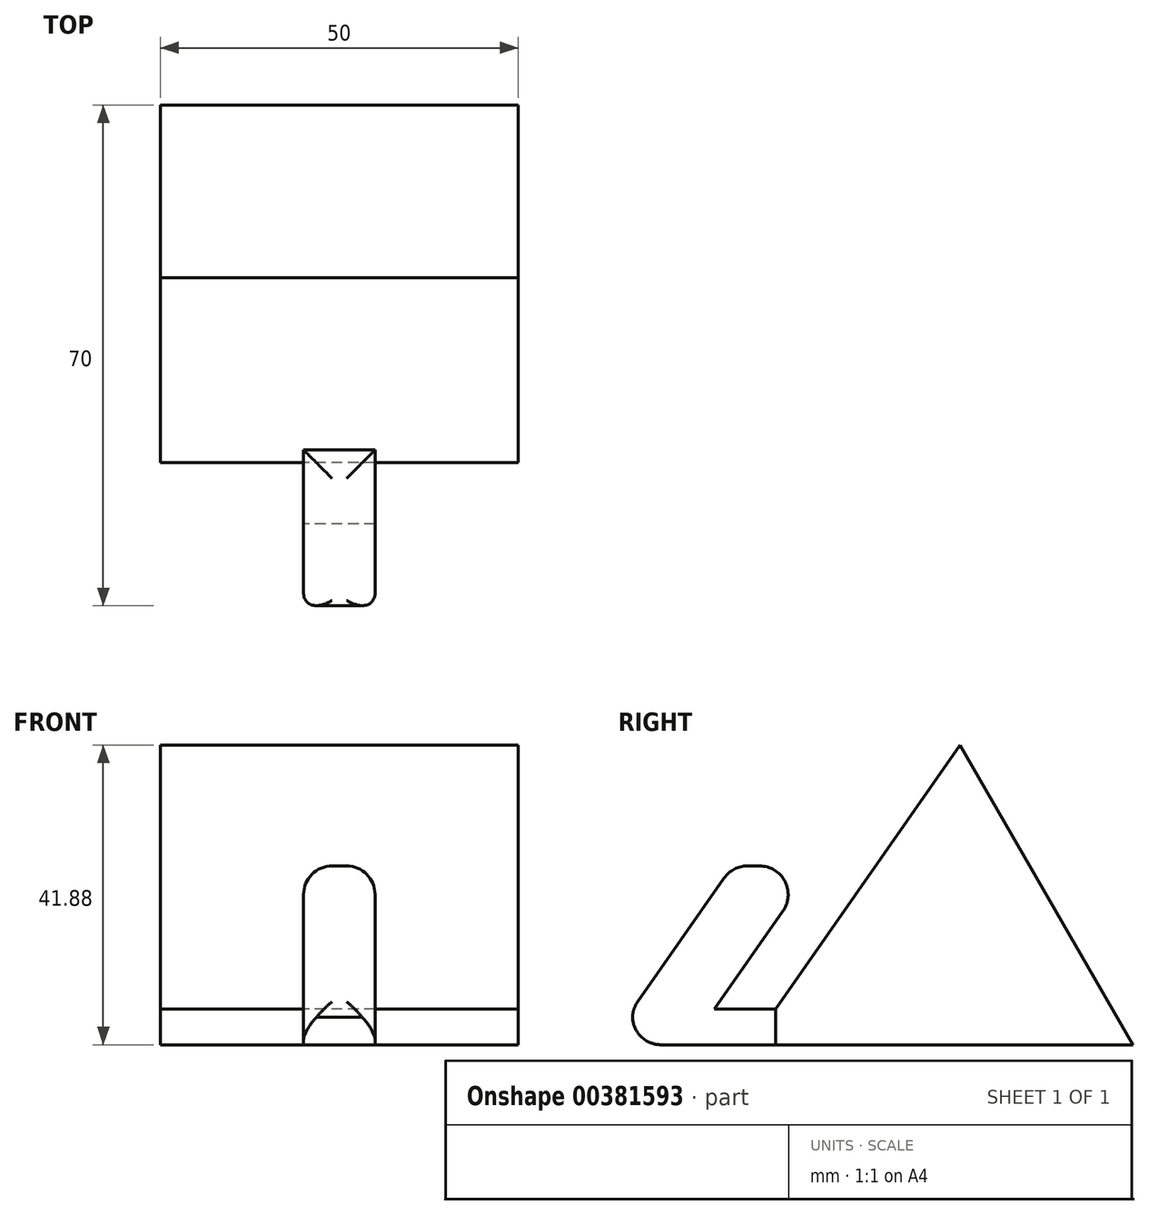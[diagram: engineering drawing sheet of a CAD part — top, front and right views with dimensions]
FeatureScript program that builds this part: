
annotation { "Feature Type Name" : "Feature", "Feature Type Description" : "" }
export const myFeature = defineFeature(function(context is Context, id is Id, definition is map)
    precondition{}
    {
        {
            var Q0;
            Q0=qCreatedBy(makeId("Right.planeOp"),FACE);
            var sketch = newSketch(context, id + "F0", { "sketchPlane" : qUnion([Q0])});
            skLineSegment(sketch, "E0.top", {"start": v(0, 5) * mm, "end": v(-8.55, 5) * mm});
            skPoint(sketch, "E0.middle", {"position": v(0, 0) * mm});
            skLineSegment(sketch, "E1", {"start": v(0, 5) * mm, "end": v(14, 25) * mm});
            skLineSegment(sketch, "E2", {"start": v(5.46, 25) * mm, "end": v(-8.55, 5) * mm});
            skLineSegment(sketch, "E3", {"start": v(-20, 5) * mm, "end": v(-6, 25) * mm});
            skLineSegment(sketch, "E4", {"start": v(-6, 25) * mm, "end": v(5.46, 25) * mm});
            skLineSegment(sketch, "E5", {"start": v(-20, 0) * mm, "end": v(0, 0) * mm});
            skLineSegment(sketch, "E6", {"start": v(50, 0) * mm, "end": v(0, 0) * mm});
            skLineSegment(sketch, "E7", {"start": v(-20, 0) * mm, "end": v(-20, 5) * mm});
            skLineSegment(sketch, "E8", {"start": v(14, 25) * mm, "end": v(25.82, 41.88) * mm});
            skLineSegment(sketch, "E9", {"start": v(25.82, 41.88) * mm, "end": v(50, 0) * mm});
            skLineSegment(sketch, "E10", {"start": v(0, 5) * mm, "end": v(0, 0) * mm});
            skSolve(sketch);
        }
        {
            var Q0;
            Q0=makeQuery(id+"F0.imprint","IMPRINT",FACE,{"disambiguationData":[TD([[makeQuery(id+"F0.imprint","IMPRINT",EDGE,{"derivedFrom":sQuery(id+"F0.wireOp",EDGE,"E0.top")}),1.0]])]});
            extrude(context, id + "F1", {"entities" : qUnion([Q0]), "endBound" : BoundingType.SYMMETRIC, "depth" : 10 * mm, "offsetDistance" : 25 * mm});
        }
        {
            var Q0;
            Q0=makeQuery(id+"F0.imprint","IMPRINT",FACE,{"disambiguationData":[TD([[makeQuery(id+"F0.imprint","IMPRINT",EDGE,{"derivedFrom":sQuery(id+"F0.wireOp",EDGE,"E1")}),-1.0]])]});
            extrude(context, id + "F2", {"entities" : qUnion([Q0]), "operationType" : NewBodyOperationType.ADD, "depth" : 25 * mm, "offsetDistance" : 25 * mm, "hasSecondDirection" : true, "secondDirectionOppositeDirection" : true, "secondDirectionDepth" : 25 * mm});
        }
        {
            var Q0;
            Q0=makeQuery(id+"F1.opExtrude","SWEPT_FACE",FACE,{"disambiguationData":[OSD([sQuery(id+"F0.wireOp",EDGE,"E3")])]});
            var Q1;
            Q1=makeQuery(id+"F1.opExtrude","SWEPT_FACE",FACE,{"disambiguationData":[OSD([sQuery(id+"F0.wireOp",EDGE,"E4")])]});
            var Q2;
            Q2=makeQuery(id+"F1.opExtrude","SWEPT_EDGE",EDGE,{"disambiguationData":[OSD([sQuery(id+"F0.wireOp",EDGE,"E5"),sQuery(id+"F0.wireOp",EDGE,"E7")])]});
            fillet(context, id + "F3", {"entities" : qUnion([Q0, Q1, Q2]), "radius" : 4 * mm, "tangentPropagation" : true, "allowEdgeOverflow" : false});
        }
    });
